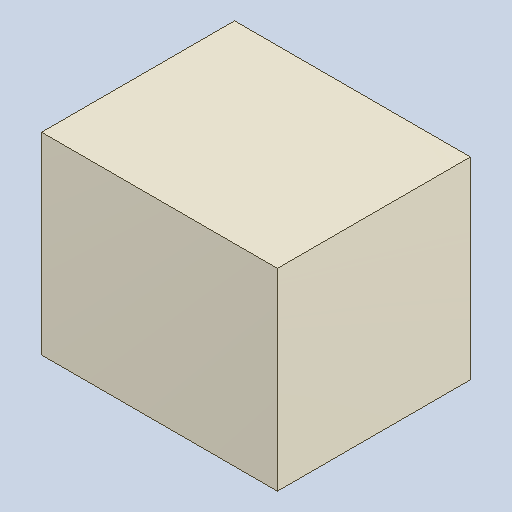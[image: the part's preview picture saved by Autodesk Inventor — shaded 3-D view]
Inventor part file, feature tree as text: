
AUTODESK INVENTOR PART (.ipt)
format: ipt  version: 2023.4 (Build 274418000, 418)  size: 81,920 bytes
history: native  units: mm
features: extrude x1
ambient origin geometry x8: Origin, YZ Plane, XZ Plane, XY Plane, X Axis, Y Axis, Z Axis, Center Point
bodies: Solid1 (feature_tree)
feature tree (1):
  extrude  "Extruded_16"  [1 undecoded]
note: 1 required parameter value undecoded (feature->parameter linkage not recoverable at this tier; creation-order binding heuristic only, values carry confidence <= 0.55)
